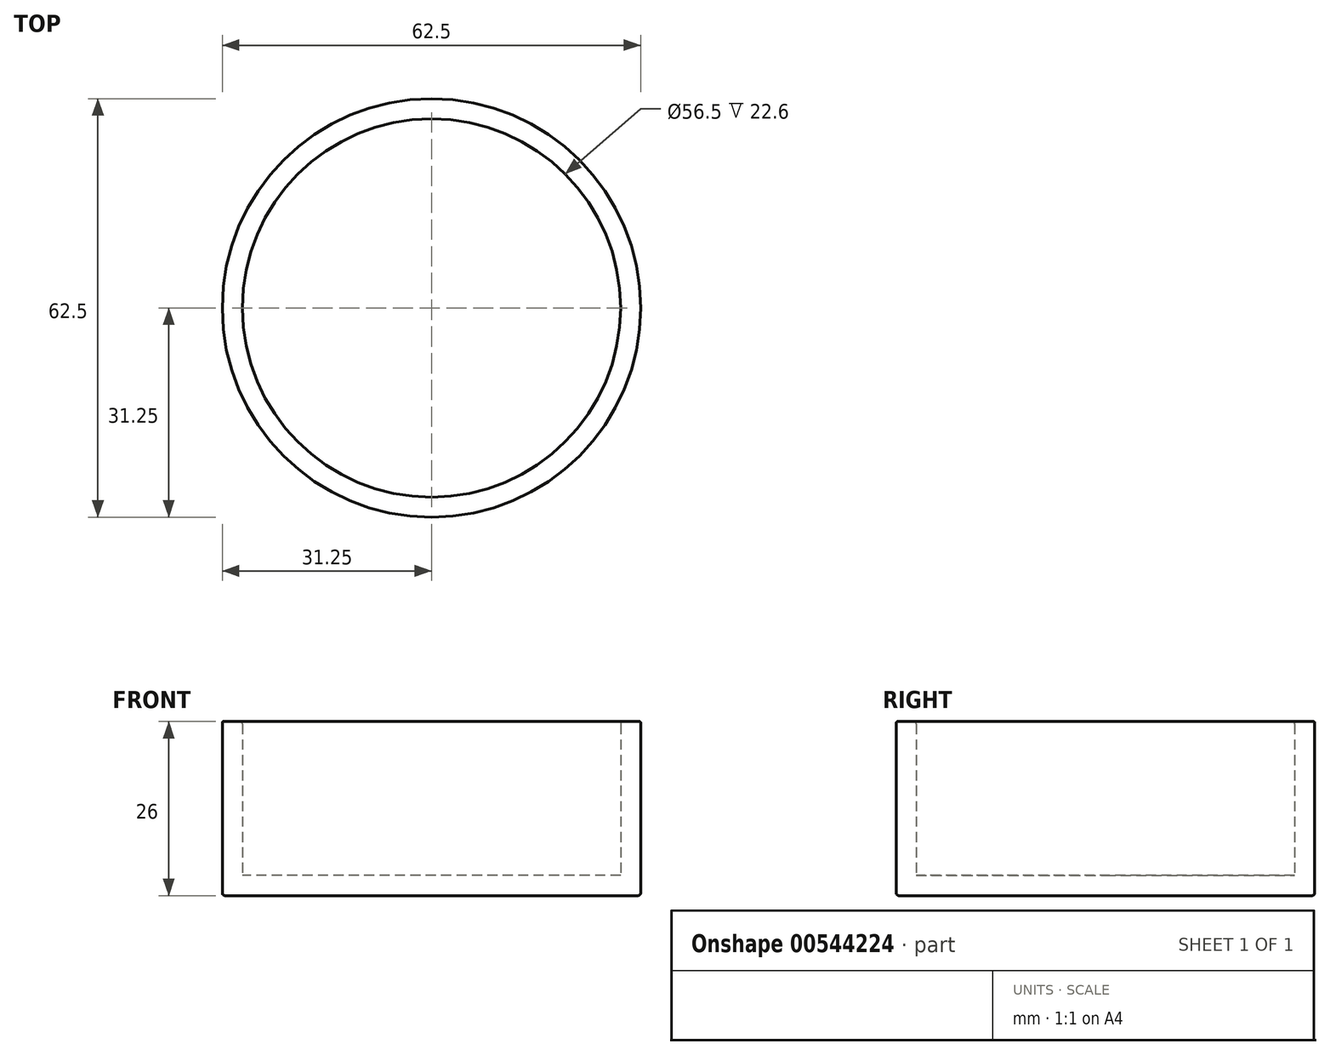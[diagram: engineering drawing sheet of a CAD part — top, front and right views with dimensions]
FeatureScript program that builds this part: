
annotation { "Feature Type Name" : "Feature", "Feature Type Description" : "" }
export const myFeature = defineFeature(function(context is Context, id is Id, definition is map)
    precondition{}
    {
        {
            var Q0;
            Q0=qCreatedBy(makeId("Top.planeOp"),FACE);
            var sketch = newSketch(context, id + "F0", { "sketchPlane" : qUnion([Q0])});
            skCircle(sketch, "E0", {"center": v(0, 0) * mm, "radius": 31.25 * mm});
            skSolve(sketch);
        }
        {
            var Q0;
            Q0=makeQuery(id+"F0.imprint","IMPRINT",FACE,{"disambiguationData":[TD([[makeQuery(id+"F0.imprint","IMPRINT",EDGE,{"derivedFrom":sQuery(id+"F0.wireOp",EDGE,"E0")}),1.0]])]});
            extrude(context, id + "F1", {"entities" : qUnion([Q0]), "depth" : 3 * mm, "offsetDistance" : 25 * mm});
        }
        {
            var Q0;
            Q0=makeQuery(id+"F1.opExtrude","CAP_FACE",FACE,{"disambiguationData":[OSD([sQuery(id+"F0.wireOp",EDGE,"E0")])],"isStart":false});
            var sketch = newSketch(context, id + "F2", { "sketchPlane" : qUnion([Q0])});
            skCircle(sketch, "E1", {"center": v(0, 0) * mm, "radius": 28.25 * mm});
            skSolve(sketch);
        }
        {
            var Q0;
            Q0=makeQuery(id+"F2.imprint","IMPRINT",FACE,{"disambiguationData":[TD([[makeQuery(id+"F2.imprint","IMPRINT",EDGE,{"derivedFrom":sQuery(id+"F2.wireOp",EDGE,"E1")}),-1.0]])]});
            extrude(context, id + "F3", {"entities" : qUnion([Q0]), "operationType" : NewBodyOperationType.ADD, "depth" : 23 * mm, "offsetDistance" : 25 * mm});
        }
        {
            var Q0;
            Q0=makeQuery(id+"F3.opExtrude","CAP_EDGE",EDGE,{"disambiguationData":[OSD([sQuery(id+"F2.wireOp",EDGE,"E1")])],"isStart":false});
            var Q1;
            Q1=makeQuery(id+"F3.opExtrude","CAP_EDGE",EDGE,{"disambiguationData":[OSD([sQuery(id+"F2.wireOp",EDGE,"E1")])],"isStart":true});
            var Q2;
            Q2=makeQuery(id+"F1.opExtrude","CAP_EDGE",EDGE,{"disambiguationData":[OSD([sQuery(id+"F0.wireOp",EDGE,"E0")])],"isStart":true});
            fillet(context, id + "F4", {"entities" : qUnion([Q0, Q1, Q2]), "radius" : 0.4 * mm, "tangentPropagation" : true, "allowEdgeOverflow" : false});
        }
        {
            var Q0;
            Q0=makeQuery(id+"F3.opExtrude","CAP_EDGE",EDGE,{"disambiguationData":[OSD([sQuery(id+"F0.wireOp",EDGE,"E0")])],"isStart":false});
            fillet(context, id + "F5", {"entities" : qUnion([Q0]), "radius" : 0.2 * mm, "tangentPropagation" : true, "allowEdgeOverflow" : false});
        }
    });
